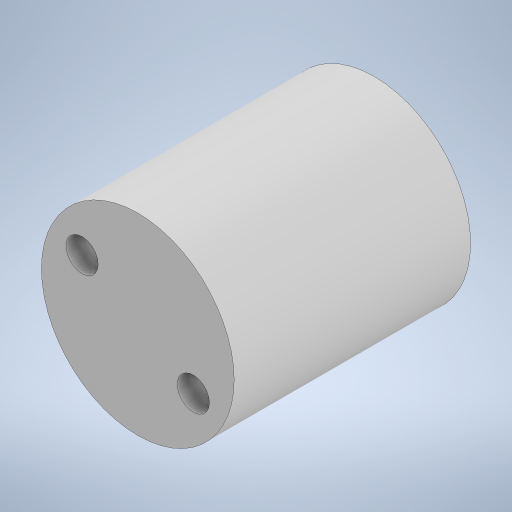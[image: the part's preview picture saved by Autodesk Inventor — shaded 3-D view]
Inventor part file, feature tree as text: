
AUTODESK INVENTOR PART (.ipt)
format: ipt  version: 2023 (Build 270158000, 158)  size: 224,256 bytes
history: native  units: in
note: dims shown in document units (in); Inventor stores cm internally (conversion verified against a paired STEP export)
features: extrude x3, sketch x2
ambient origin geometry x8: Origin, YZ Plane, XZ Plane, XY Plane, X Axis, Y Axis, Z Axis, Center Point
bodies: Body1 (feature_tree)
feature tree (5):
  sketch  "Sketch1"  dims[d3=0.125in d4=0.125in]
  extrude  "Extrusion2"  Depth=0.125in
  extrude  "Extrusion3"  Depth=0.25in TaperAngle=0.0deg
  extrude  "Extrusion4"  Depth=0.25in
  sketch  "Sketch2"  dims[d12=0.92in d13=0.0in d14=0.25in d15=0.0in d22=0.25in d23=0.5in d24=0.125in d25=0.125in d26=0.25in d27=0.0in]
